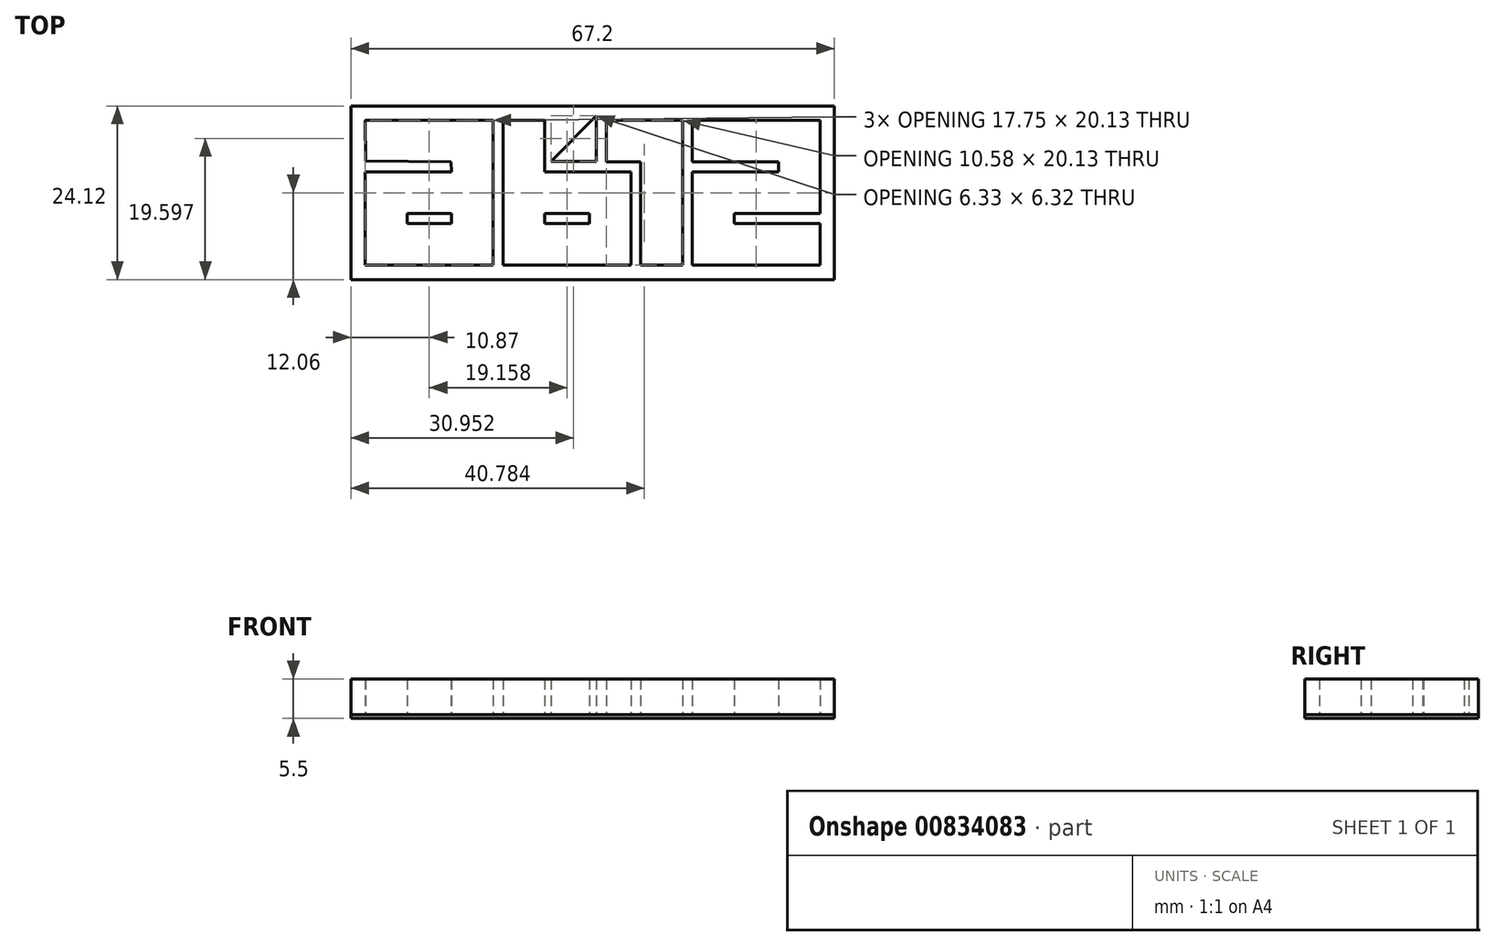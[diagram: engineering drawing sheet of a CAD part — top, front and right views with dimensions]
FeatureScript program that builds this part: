
annotation { "Feature Type Name" : "Feature", "Feature Type Description" : "" }
export const myFeature = defineFeature(function(context is Context, id is Id, definition is map)
    precondition{}
    {
        {
            var Q0;
            Q0=qCreatedBy(makeId("Top.planeOp"),FACE);
            var sketch = newSketch(context, id + "F0", { "sketchPlane" : qUnion([Q0])});
            skLineSegment(sketch, "E0", {"start": v(-31.1, 9.52) * mm, "end": v(-14.35, 9.52) * mm});
            skLineSegment(sketch, "E1", {"start": v(-14.35, 9.52) * mm, "end": v(-14.35, -9.6) * mm});
            skLineSegment(sketch, "E2", {"start": v(-14.35, -9.6) * mm, "end": v(-31.1, -9.6) * mm});
            skLineSegment(sketch, "E3", {"start": v(-31.1, -9.6) * mm, "end": v(-31.1, 2.35) * mm});
            skLineSegment(sketch, "E4", {"start": v(-31.1, 2.35) * mm, "end": v(-19.14, 2.35) * mm});
            skLineSegment(sketch, "E5", {"start": v(-19.14, 2.35) * mm, "end": v(-19.18, 4.77) * mm});
            skLineSegment(sketch, "E6", {"start": v(-19.18, 4.77) * mm, "end": v(-31.06, 4.87) * mm});
            skLineSegment(sketch, "E7", {"start": v(-19.14, -2.44) * mm, "end": v(-26.31, -2.44) * mm});
            skLineSegment(sketch, "E8", {"start": v(-26.31, -2.44) * mm, "end": v(-26.31, -4.82) * mm});
            skLineSegment(sketch, "E9", {"start": v(-26.31, -4.82) * mm, "end": v(-19.14, -4.82) * mm});
            skLineSegment(sketch, "E10", {"start": v(-19.14, -4.82) * mm, "end": v(-19.14, -2.44) * mm});
            skLineSegment(sketch, "E11", {"start": v(-11.95, 9.52) * mm, "end": v(-7.16, 9.52) * mm});
            skLineSegment(sketch, "E12", {"start": v(-7.16, 9.52) * mm, "end": v(-7.16, 2.35) * mm});
            skLineSegment(sketch, "E13", {"start": v(-7.16, 2.35) * mm, "end": v(4.8, 2.35) * mm});
            skLineSegment(sketch, "E14", {"start": v(4.8, 2.35) * mm, "end": v(4.8, -9.6) * mm});
            skLineSegment(sketch, "E15", {"start": v(4.8, -9.6) * mm, "end": v(-11.95, -9.6) * mm});
            skLineSegment(sketch, "E16", {"start": v(-11.95, -9.6) * mm, "end": v(-11.95, 9.52) * mm});
            skLineSegment(sketch, "E17", {"start": v(0.01, -2.44) * mm, "end": v(-7.16, -2.44) * mm});
            skLineSegment(sketch, "E18", {"start": v(-7.16, -2.44) * mm, "end": v(-7.16, -4.82) * mm});
            skLineSegment(sketch, "E19", {"start": v(-7.16, -4.82) * mm, "end": v(0.01, -4.82) * mm});
            skLineSegment(sketch, "E20", {"start": v(0.01, -4.82) * mm, "end": v(0.01, -2.44) * mm});
            skLineSegment(sketch, "E21", {"start": v(7.18, 4.76) * mm, "end": v(7.18, -9.6) * mm});
            skLineSegment(sketch, "E22", {"start": v(7.18, -9.6) * mm, "end": v(11.97, -9.6) * mm});
            skLineSegment(sketch, "E23", {"start": v(11.97, -9.6) * mm, "end": v(11.97, 9.52) * mm});
            skLineSegment(sketch, "E24", {"start": v(11.97, 9.52) * mm, "end": v(2.4, 9.52) * mm});
            skLineSegment(sketch, "E25", {"start": v(2.4, 9.52) * mm, "end": v(2.4, 4.76) * mm});
            skLineSegment(sketch, "E26", {"start": v(2.4, 4.76) * mm, "end": v(7.18, 4.76) * mm});
            skLineSegment(sketch, "E27", {"start": v(31.1, -2.44) * mm, "end": v(19.14, -2.44) * mm});
            skLineSegment(sketch, "E28", {"start": v(19.14, -2.44) * mm, "end": v(19.14, -4.82) * mm});
            skLineSegment(sketch, "E29", {"start": v(19.14, -4.82) * mm, "end": v(31.1, -4.82) * mm});
            skLineSegment(sketch, "E30", {"start": v(31.1, -4.82) * mm, "end": v(31.1, -9.6) * mm});
            skLineSegment(sketch, "E31", {"start": v(31.1, -9.6) * mm, "end": v(14.35, -9.6) * mm});
            skLineSegment(sketch, "E32", {"start": v(14.35, -9.6) * mm, "end": v(14.35, 2.35) * mm});
            skLineSegment(sketch, "E33", {"start": v(14.35, 2.35) * mm, "end": v(26.34, 2.35) * mm});
            skLineSegment(sketch, "E34", {"start": v(26.34, 2.35) * mm, "end": v(26.34, 4.76) * mm});
            skLineSegment(sketch, "E35", {"start": v(26.34, 4.76) * mm, "end": v(14.35, 4.76) * mm});
            skLineSegment(sketch, "E36", {"start": v(14.35, 4.76) * mm, "end": v(14.35, 9.52) * mm});
            skLineSegment(sketch, "E37", {"start": v(14.35, 9.52) * mm, "end": v(31.1, 9.52) * mm});
            skLineSegment(sketch, "E38", {"start": v(31.1, 9.52) * mm, "end": v(31.1, -2.44) * mm});
            skLineSegment(sketch, "E39", {"start": v(0.01, 4.85) * mm, "end": v(-0.02, 9.45) * mm});
            skLineSegment(sketch, "E40", {"start": v(-0.02, 9.45) * mm, "end": v(-4.6, 4.84) * mm});
            skLineSegment(sketch, "E41", {"start": v(-4.6, 4.84) * mm, "end": v(0.01, 4.85) * mm});
            skLineSegment(sketch, "E42.0", {"start": v(13.85, 4.26) * mm, "end": v(13.85, 10.02) * mm});
            skLineSegment(sketch, "E42.1", {"start": v(19.64, -4.32) * mm, "end": v(31.6, -4.32) * mm});
            skLineSegment(sketch, "E42.2", {"start": v(19.64, -2.94) * mm, "end": v(19.64, -4.32) * mm});
            skLineSegment(sketch, "E42.3", {"start": v(31.6, -2.94) * mm, "end": v(19.64, -2.94) * mm});
            skLineSegment(sketch, "E42.4", {"start": v(31.6, 10.02) * mm, "end": v(31.6, -2.94) * mm});
            skLineSegment(sketch, "E42.5", {"start": v(31.6, -4.32) * mm, "end": v(31.6, -10.1) * mm});
            skLineSegment(sketch, "E42.6", {"start": v(13.85, 10.02) * mm, "end": v(31.6, 10.02) * mm});
            skLineSegment(sketch, "E42.7", {"start": v(31.6, -10.1) * mm, "end": v(13.85, -10.1) * mm});
            skLineSegment(sketch, "E42.8", {"start": v(13.85, -10.1) * mm, "end": v(13.85, 2.85) * mm});
            skLineSegment(sketch, "E42.9", {"start": v(13.85, 2.85) * mm, "end": v(25.84, 2.85) * mm});
            skLineSegment(sketch, "E42.10", {"start": v(25.84, 2.85) * mm, "end": v(25.84, 4.26) * mm});
            skLineSegment(sketch, "E42.11", {"start": v(25.84, 4.26) * mm, "end": v(13.85, 4.26) * mm});
            skLineSegment(sketch, "E43.0", {"start": v(12.47, -10.1) * mm, "end": v(12.47, 10.02) * mm});
            skLineSegment(sketch, "E43.1", {"start": v(1.9, 10.02) * mm, "end": v(1.9, 4.26) * mm});
            skLineSegment(sketch, "E43.2", {"start": v(1.9, 4.26) * mm, "end": v(6.68, 4.26) * mm});
            skLineSegment(sketch, "E43.3", {"start": v(12.47, 10.02) * mm, "end": v(1.9, 10.02) * mm});
            skLineSegment(sketch, "E43.4", {"start": v(6.68, 4.26) * mm, "end": v(6.68, -10.1) * mm});
            skLineSegment(sketch, "E43.5", {"start": v(6.68, -10.1) * mm, "end": v(12.47, -10.1) * mm});
            skLineSegment(sketch, "E44.0", {"start": v(0.48, 10.66) * mm, "end": v(-5.81, 4.33) * mm});
            skLineSegment(sketch, "E44.1", {"start": v(0.52, 4.35) * mm, "end": v(0.48, 10.66) * mm});
            skLineSegment(sketch, "E44.2", {"start": v(-5.81, 4.33) * mm, "end": v(0.52, 4.35) * mm});
            skLineSegment(sketch, "E45.0", {"start": v(-12.45, -10.1) * mm, "end": v(-12.45, 10.02) * mm});
            skLineSegment(sketch, "E45.1", {"start": v(-6.66, 10.02) * mm, "end": v(-6.66, 2.85) * mm});
            skLineSegment(sketch, "E45.2", {"start": v(-6.66, 2.85) * mm, "end": v(5.3, 2.85) * mm});
            skLineSegment(sketch, "E45.3", {"start": v(-12.45, 10.02) * mm, "end": v(-6.66, 10.02) * mm});
            skLineSegment(sketch, "E45.4", {"start": v(5.3, 2.85) * mm, "end": v(5.3, -10.1) * mm});
            skLineSegment(sketch, "E45.5", {"start": v(5.3, -10.1) * mm, "end": v(-12.45, -10.1) * mm});
            skLineSegment(sketch, "E46", {"start": v(-31.1, 9.52) * mm, "end": v(-31.06, 4.87) * mm});
            skLineSegment(sketch, "E47.0", {"start": v(-31.6, 10.02) * mm, "end": v(-31.55, 4.38) * mm});
            skLineSegment(sketch, "E47.1", {"start": v(-19.67, 4.27) * mm, "end": v(-31.55, 4.38) * mm});
            skLineSegment(sketch, "E47.2", {"start": v(-31.6, 10.02) * mm, "end": v(-13.85, 10.02) * mm});
            skLineSegment(sketch, "E47.3", {"start": v(-19.65, 2.85) * mm, "end": v(-19.67, 4.27) * mm});
            skLineSegment(sketch, "E47.4", {"start": v(-13.85, 10.02) * mm, "end": v(-13.85, -10.1) * mm});
            skLineSegment(sketch, "E47.5", {"start": v(-13.85, -10.1) * mm, "end": v(-31.6, -10.1) * mm});
            skLineSegment(sketch, "E47.6", {"start": v(-31.6, -10.1) * mm, "end": v(-31.6, 2.85) * mm});
            skLineSegment(sketch, "E47.7", {"start": v(-31.6, 2.85) * mm, "end": v(-19.65, 2.85) * mm});
            skLineSegment(sketch, "E48.bottom", {"start": v(-33.6, 12.02) * mm, "end": v(33.6, 12.02) * mm});
            skLineSegment(sketch, "E48.top", {"start": v(-33.6, -12.1) * mm, "end": v(33.6, -12.1) * mm});
            skLineSegment(sketch, "E48.left", {"start": v(-33.6, 12.02) * mm, "end": v(-33.6, -12.1) * mm});
            skLineSegment(sketch, "E48.right", {"start": v(33.6, 12.02) * mm, "end": v(33.6, -12.1) * mm});
            skLineSegment(sketch, "E49.0", {"start": v(-19.64, -2.94) * mm, "end": v(-25.81, -2.94) * mm});
            skLineSegment(sketch, "E49.1", {"start": v(-19.64, -4.32) * mm, "end": v(-19.64, -2.94) * mm});
            skLineSegment(sketch, "E49.2", {"start": v(-25.81, -4.32) * mm, "end": v(-19.64, -4.32) * mm});
            skLineSegment(sketch, "E49.3", {"start": v(-25.81, -2.94) * mm, "end": v(-25.81, -4.32) * mm});
            skLineSegment(sketch, "E50.0", {"start": v(-0.49, -2.94) * mm, "end": v(-6.66, -2.94) * mm});
            skLineSegment(sketch, "E50.1", {"start": v(-0.49, -4.32) * mm, "end": v(-0.49, -2.94) * mm});
            skLineSegment(sketch, "E50.2", {"start": v(-6.66, -4.32) * mm, "end": v(-0.49, -4.32) * mm});
            skLineSegment(sketch, "E50.3", {"start": v(-6.66, -2.94) * mm, "end": v(-6.66, -4.32) * mm});
            skSolve(sketch);
        }
        {
            var Q0;
            Q0=makeQuery(id+"F0.imprint","IMPRINT",FACE,{"disambiguationData":[TD([[makeQuery(id+"F0.imprint","IMPRINT",EDGE,{"derivedFrom":sQuery(id+"F0.wireOp",EDGE,"E42.0")}),1.0]])]});
            extrude(context, id + "F1", {"entities" : qUnion([Q0]), "depth" : 5 * mm, "offsetDistance" : 25 * mm});
        }
        {
            var Q0;
            Q0=makeQuery(id+"F0.imprint","IMPRINT",FACE,{"disambiguationData":[TD([[makeQuery(id+"F0.imprint","IMPRINT",EDGE,{"derivedFrom":sQuery(id+"F0.wireOp",EDGE,"E50.0")}),1.0]])]});
            var Q1;
            Q1=makeQuery(id+"F0.imprint","IMPRINT",FACE,{"disambiguationData":[TD([[makeQuery(id+"F0.imprint","IMPRINT",EDGE,{"derivedFrom":sQuery(id+"F0.wireOp",EDGE,"E49.0")}),1.0]])]});
            var Q2;
            Q2=sQuery(id+"F0.wireOp",EDGE,"E49.0");
            var Q3;
            Q3=sQuery(id+"F0.wireOp",EDGE,"E49.2");
            extrude(context, id + "F2", {"entities" : qUnion([Q0, Q1]), "surfaceEntities" : qUnion([Q2, Q3]), "depth" : 5 * mm, "offsetDistance" : 25 * mm});
        }
        {
            var Q0;
            Q0=makeQuery(id+"F0.imprint","IMPRINT",FACE,{"disambiguationData":[TD([[makeQuery(id+"F0.imprint","IMPRINT",EDGE,{"derivedFrom":sQuery(id+"F0.wireOp",EDGE,"E42.0")}),1.0]])]});
            var sketch = newSketch(context, id + "F3", { "sketchPlane" : qUnion([Q0])});
            skLineSegment(sketch, "E51.bottom", {"start": v(33.6, -12.1) * mm, "end": v(-33.6, -12.1) * mm});
            skLineSegment(sketch, "E51.top", {"start": v(33.6, 12.02) * mm, "end": v(-33.6, 12.02) * mm});
            skLineSegment(sketch, "E51.left", {"start": v(33.6, -12.1) * mm, "end": v(33.6, 12.02) * mm});
            skLineSegment(sketch, "E51.right", {"start": v(-33.6, -12.1) * mm, "end": v(-33.6, 12.02) * mm});
            skSolve(sketch);
        }
        {
            var Q0;
            Q0 = qSketchRegion(id + "F3", true);
            extrude(context, id + "F4", {"entities" : qUnion([Q0]), "oppositeDirection" : true, "depth" : 0.5 * mm, "offsetDistance" : 25 * mm});
        }
    });
